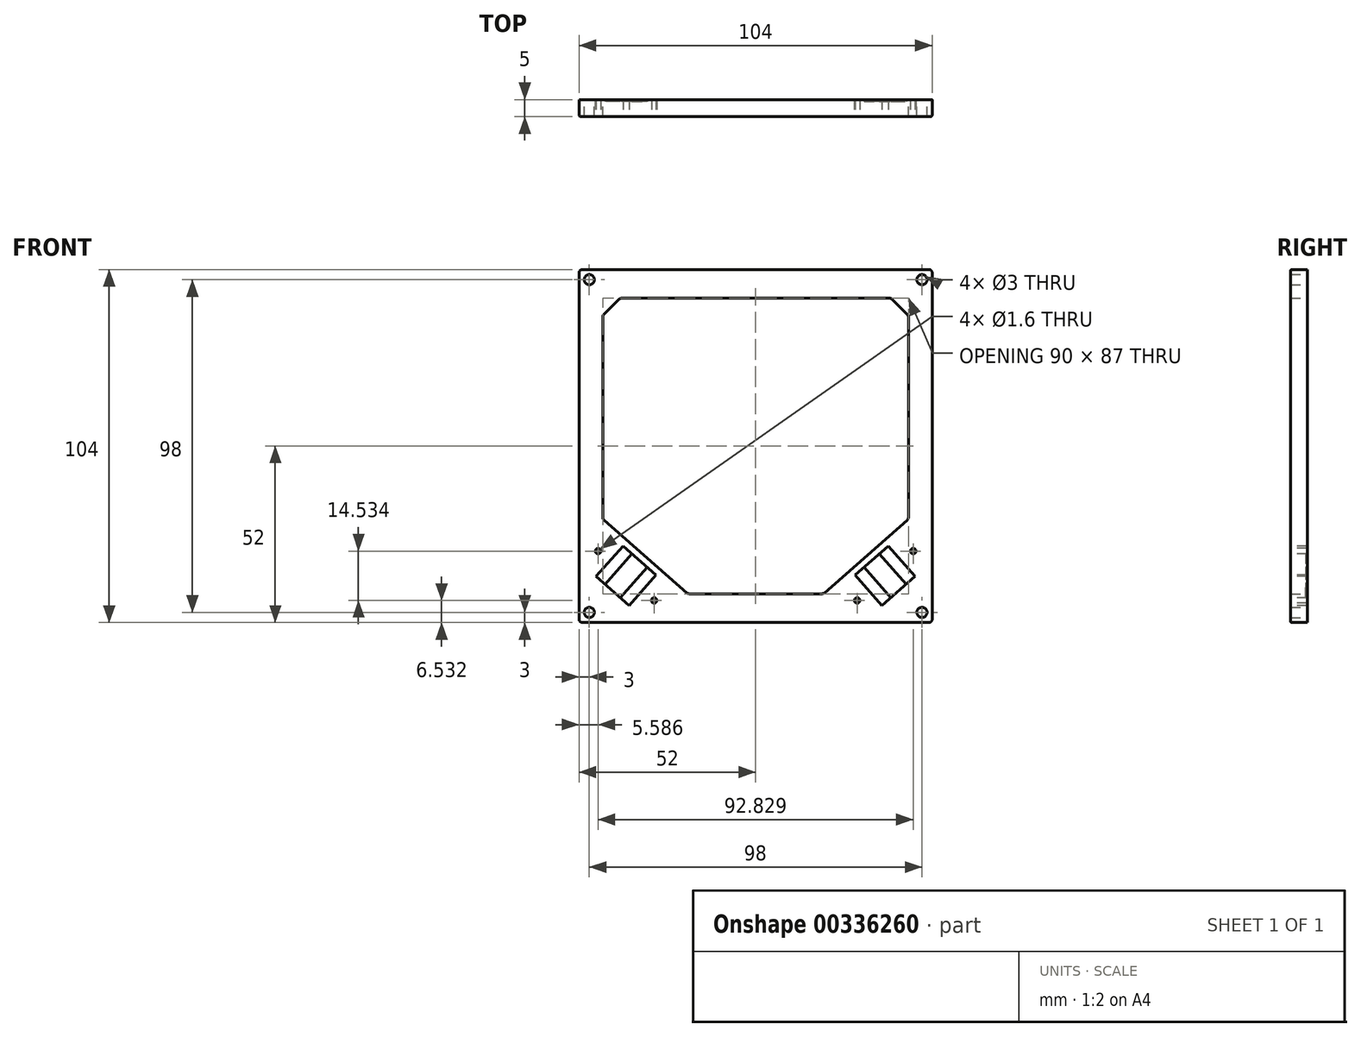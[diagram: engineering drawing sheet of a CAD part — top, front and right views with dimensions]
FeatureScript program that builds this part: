
annotation { "Feature Type Name" : "Feature", "Feature Type Description" : "" }
export const myFeature = defineFeature(function(context is Context, id is Id, definition is map)
    precondition{}
    {
        {
            var Q0;
            Q0=qCreatedBy(makeId("Front.planeOp"),FACE);
            var sketch = newSketch(context, id + "F0", { "sketchPlane" : qUnion([Q0])});
            skLineSegment(sketch, "E0.bottom", {"start": v(-52, 52) * mm, "end": v(52, 52) * mm});
            skLineSegment(sketch, "E0.top", {"start": v(-52, -52) * mm, "end": v(52, -52) * mm});
            skLineSegment(sketch, "E0.left", {"start": v(-52, 52) * mm, "end": v(-52, -52) * mm});
            skLineSegment(sketch, "E0.right", {"start": v(52, 52) * mm, "end": v(52, -52) * mm});
            skCircle(sketch, "E1", {"center": v(-49, 49) * mm, "radius": 1.5 * mm});
            skCircle(sketch, "E2", {"center": v(49, 49) * mm, "radius": 1.5 * mm});
            skCircle(sketch, "E3", {"center": v(-49, -49) * mm, "radius": 1.5 * mm});
            skCircle(sketch, "E4", {"center": v(49, -49) * mm, "radius": 1.5 * mm});
            skCircle(sketch, "E5", {"center": v(-41, -41) * mm, "radius": 2.5 * mm, "construction": true});
            skCircle(sketch, "E6", {"center": v(41, -41) * mm, "radius": 2.5 * mm, "construction": true});
            skSolve(sketch);
        }
        {
            var Q0;
            Q0=makeQuery(id+"F0.imprint","IMPRINT",FACE,{"disambiguationData":[TD([[makeQuery(id+"F0.imprint","IMPRINT",EDGE,{"derivedFrom":sQuery(id+"F0.wireOp",EDGE,"E0.bottom")}),-1.0]])]});
            extrude(context, id + "F1", {"entities" : qUnion([Q0]), "depth" : 5 * mm});
        }
        {
            var Q0;
            Q0=qCreatedBy(makeId("Front.planeOp"),FACE);
            var sketch = newSketch(context, id + "F2", { "sketchPlane" : qUnion([Q0])});
            skLineSegment(sketch, "E7", {"start": v(-40, 43.5) * mm, "end": v(40, 43.5) * mm});
            skLineSegment(sketch, "E8", {"start": v(40, 43.5) * mm, "end": v(45, 38.5) * mm});
            skLineSegment(sketch, "E9", {"start": v(45, 38.5) * mm, "end": v(45, -21.5) * mm});
            skLineSegment(sketch, "E10", {"start": v(45, -21.5) * mm, "end": v(20, -43.5) * mm});
            skLineSegment(sketch, "E11", {"start": v(20, -43.5) * mm, "end": v(-20, -43.5) * mm});
            skLineSegment(sketch, "E12", {"start": v(-20, -43.5) * mm, "end": v(-45, -21.5) * mm});
            skLineSegment(sketch, "E13", {"start": v(-45, -21.5) * mm, "end": v(-45, 38.5) * mm});
            skLineSegment(sketch, "E14", {"start": v(-45, 38.5) * mm, "end": v(-40, 43.5) * mm});
            skSolve(sketch);
        }
        {
            var Q0;
            Q0=qSketchRegion(id+"F2",true);
            var Q1;
            Q1=makeQuery(id+"F1.opExtrude","CAP_FACE",FACE,{"disambiguationData":[OSD([sQuery(id+"F0.wireOp",EDGE,"E0.bottom"),sQuery(id+"F0.wireOp",EDGE,"E0.top"),sQuery(id+"F0.wireOp",EDGE,"E0.left"),sQuery(id+"F0.wireOp",EDGE,"E0.right"),sQuery(id+"F0.wireOp",EDGE,"E1"),sQuery(id+"F0.wireOp",EDGE,"E2"),sQuery(id+"F0.wireOp",EDGE,"E3"),sQuery(id+"F0.wireOp",EDGE,"E4")])],"isStart":false});
            extrude(context, id + "F3", {"entities" : qUnion([Q0, Q1]), "operationType" : NewBodyOperationType.REMOVE, "depth" : 25 * mm});
        }
        {
            var Q0;
            Q0=makeQuery(id+"F1.opExtrude","CAP_FACE",FACE,{"disambiguationData":[OSD([sQuery(id+"F0.wireOp",EDGE,"E0.bottom"),sQuery(id+"F0.wireOp",EDGE,"E0.top"),sQuery(id+"F0.wireOp",EDGE,"E0.left"),sQuery(id+"F0.wireOp",EDGE,"E0.right"),sQuery(id+"F0.wireOp",EDGE,"E1"),sQuery(id+"F0.wireOp",EDGE,"E2"),sQuery(id+"F0.wireOp",EDGE,"E3"),sQuery(id+"F0.wireOp",EDGE,"E4")])],"isStart":false});
            var sketch = newSketch(context, id + "F4", { "sketchPlane" : qUnion([Q0])});
            skLineSegment(sketch, "E15", {"start": v(-39.07, -29.4) * mm, "end": v(-29.31, -38) * mm});
            skLineSegment(sketch, "E16", {"start": v(-29.31, -38) * mm, "end": v(-37.24, -47) * mm});
            skLineSegment(sketch, "E17", {"start": v(-37.24, -47) * mm, "end": v(-47, -38.41) * mm});
            skLineSegment(sketch, "E18", {"start": v(-47, -38.41) * mm, "end": v(-39.07, -29.4) * mm});
            skCircle(sketch, "E19", {"center": v(-46.41, -30.93) * mm, "radius": 1 * mm, "construction": true});
            skCircle(sketch, "E20", {"center": v(-29.9, -45.47) * mm, "radius": 1 * mm, "construction": true});
            skLineSegment(sketch, "E21", {"start": v(-41.1, -24.93) * mm, "end": v(-15.3, -47.64) * mm, "construction": true});
            skLineSegment(sketch, "E22", {"start": v(0, -14.2) * mm, "end": v(0, -66.24) * mm, "construction": true});
            skCircle(sketch, "E23.MirrorC", {"center": v(29.9, -45.47) * mm, "radius": 1 * mm, "construction": true});
            skCircle(sketch, "E24.MirrorC", {"center": v(46.41, -30.93) * mm, "radius": 1 * mm, "construction": true});
            skLineSegment(sketch, "E25.MirrorCS", {"start": v(39.07, -29.4) * mm, "end": v(29.31, -38) * mm});
            skLineSegment(sketch, "E26.MirrorCS", {"start": v(47, -38.41) * mm, "end": v(39.07, -29.4) * mm});
            skLineSegment(sketch, "E27.MirrorCS", {"start": v(37.24, -47) * mm, "end": v(47, -38.41) * mm});
            skLineSegment(sketch, "E28.MirrorCS", {"start": v(29.31, -38) * mm, "end": v(37.24, -47) * mm});
            skSolve(sketch);
        }
        {
            var Q0;
            Q0 = qSketchRegion(id + "F4", true);
            extrude(context, id + "F5", {"entities" : qUnion([Q0]), "operationType" : NewBodyOperationType.REMOVE, "oppositeDirection" : true, "depth" : 4.5 * mm});
        }
        {
            var Q0;
            Q0=makeQuery(id+"F5.boolean.opBoolean","COPY",FACE,{"derivedFrom":makeQuery(id+"F5.opExtrude","CAP_FACE",FACE,{"disambiguationData":[OSD([sQuery(id+"F4.wireOp",EDGE,"E15"),sQuery(id+"F4.wireOp",EDGE,"E16"),sQuery(id+"F4.wireOp",EDGE,"E17"),sQuery(id+"F4.wireOp",EDGE,"E18")])],"isStart":false})});
            var sketch = newSketch(context, id + "F6", { "sketchPlane" : qUnion([Q0])});
            skLineSegment(sketch, "E29", {"start": v(-47, -38.41) * mm, "end": v(-39.07, -29.4) * mm});
            skLineSegment(sketch, "E30", {"start": v(-39.07, -29.4) * mm, "end": v(-36.44, -31.72) * mm});
            skLineSegment(sketch, "E31", {"start": v(-36.44, -31.72) * mm, "end": v(-44.37, -40.72) * mm});
            skLineSegment(sketch, "E32", {"start": v(-44.37, -40.72) * mm, "end": v(-47, -38.41) * mm});
            skLineSegment(sketch, "E33", {"start": v(-31.94, -35.68) * mm, "end": v(-39.87, -44.69) * mm});
            skLineSegment(sketch, "E34", {"start": v(-39.87, -44.69) * mm, "end": v(-37.24, -47) * mm});
            skLineSegment(sketch, "E35", {"start": v(-37.24, -47) * mm, "end": v(-29.31, -38) * mm});
            skLineSegment(sketch, "E36", {"start": v(-29.31, -38) * mm, "end": v(-31.94, -35.68) * mm});
            skLineSegment(sketch, "E37", {"start": v(0, -27.95) * mm, "end": v(0, -63.87) * mm, "construction": true});
            skLineSegment(sketch, "E38.MirrorCS", {"start": v(29.31, -38) * mm, "end": v(31.94, -35.68) * mm});
            skLineSegment(sketch, "E39.MirrorCS", {"start": v(44.37, -40.72) * mm, "end": v(47, -38.41) * mm});
            skLineSegment(sketch, "E40.MirrorCS", {"start": v(39.07, -29.4) * mm, "end": v(36.44, -31.72) * mm});
            skLineSegment(sketch, "E41.MirrorCS", {"start": v(39.87, -44.69) * mm, "end": v(37.24, -47) * mm});
            skLineSegment(sketch, "E42.MirrorCS", {"start": v(47, -38.41) * mm, "end": v(39.07, -29.4) * mm});
            skLineSegment(sketch, "E43.MirrorCS", {"start": v(37.24, -47) * mm, "end": v(29.31, -38) * mm});
            skLineSegment(sketch, "E44.MirrorCS", {"start": v(31.94, -35.68) * mm, "end": v(39.87, -44.69) * mm});
            skLineSegment(sketch, "E45.MirrorCS", {"start": v(36.44, -31.72) * mm, "end": v(44.37, -40.72) * mm});
            skSolve(sketch);
        }
        {
            var Q0;
            Q0 = qSketchRegion(id + "F6", true);
            extrude(context, id + "F7", {"entities" : qUnion([Q0]), "operationType" : NewBodyOperationType.REMOVE, "oppositeDirection" : true, "depth" : 2 * mm});
        }
        {
            var Q0;
            Q0=sQuery(id+"F4.wireOp",VERTEX,"E19.center");
            var Q1;
            Q1=sQuery(id+"F4.wireOp",VERTEX,"E20.center");
            var Q2;
            Q2=sQuery(id+"F4.wireOp",VERTEX,"E23.MirrorC.center");
            var Q3;
            Q3=sQuery(id+"F4.wireOp",VERTEX,"E24.MirrorC.center");
            var Q4;
            Q4=makeQuery(id+"F1.opExtrude","SWEPT_BODY",BODY,{"disambiguationData":[OSD([sQuery(id+"F0.wireOp",EDGE,"E0.bottom"),sQuery(id+"F0.wireOp",EDGE,"E0.top"),sQuery(id+"F0.wireOp",EDGE,"E0.left"),sQuery(id+"F0.wireOp",EDGE,"E0.right"),sQuery(id+"F0.wireOp",EDGE,"E1"),sQuery(id+"F0.wireOp",EDGE,"E2"),sQuery(id+"F0.wireOp",EDGE,"E3"),sQuery(id+"F0.wireOp",EDGE,"E4")])]});
            hole(context, id + "F8", {"style" : HoleStyle.SIMPLE, "endStyle" : HoleEndStyle.BLIND, "holeDiameter" : 1.6 * mm, "holeDepth" : 15 * mm, "tappedDepth" : 12 * mm, "tapClearance" : 3, "locations" : qUnion([Q0, Q1, Q2, Q3]), "scope" : qUnion([Q4])});
        }
        {
            var Q0;
            Q0=makeQuery(id+"F1.opExtrude","SWEPT_EDGE",EDGE,{"disambiguationData":[OSD([sQuery(id+"F0.wireOp",EDGE,"E0.bottom"),sQuery(id+"F0.wireOp",EDGE,"E0.left")])]});
            var Q1;
            Q1=makeQuery(id+"F1.opExtrude","SWEPT_EDGE",EDGE,{"disambiguationData":[OSD([sQuery(id+"F0.wireOp",EDGE,"E0.bottom"),sQuery(id+"F0.wireOp",EDGE,"E0.right")])]});
            var Q2;
            Q2=makeQuery(id+"F1.opExtrude","SWEPT_EDGE",EDGE,{"disambiguationData":[OSD([sQuery(id+"F0.wireOp",EDGE,"E0.top"),sQuery(id+"F0.wireOp",EDGE,"E0.right")])]});
            var Q3;
            Q3=makeQuery(id+"F1.opExtrude","SWEPT_EDGE",EDGE,{"disambiguationData":[OSD([sQuery(id+"F0.wireOp",EDGE,"E0.top"),sQuery(id+"F0.wireOp",EDGE,"E0.left")])]});
            var Q4;
            Q4=makeQuery(id+"F3.boolean.opBoolean","COPY",EDGE,{"derivedFrom":makeQuery(id+"F3.opExtrude","SWEPT_EDGE",EDGE,{"disambiguationData":[OSD([sQuery(id+"F2.wireOp",EDGE,"E12"),sQuery(id+"F2.wireOp",EDGE,"E13")])]})});
            var Q5;
            Q5=makeQuery(id+"F3.boolean.opBoolean","COPY",EDGE,{"derivedFrom":makeQuery(id+"F3.opExtrude","SWEPT_EDGE",EDGE,{"disambiguationData":[OSD([sQuery(id+"F2.wireOp",EDGE,"E11"),sQuery(id+"F2.wireOp",EDGE,"E12")])]})});
            var Q6;
            Q6=makeQuery(id+"F3.boolean.opBoolean","COPY",EDGE,{"derivedFrom":makeQuery(id+"F3.opExtrude","SWEPT_EDGE",EDGE,{"disambiguationData":[OSD([sQuery(id+"F2.wireOp",EDGE,"E10"),sQuery(id+"F2.wireOp",EDGE,"E11")])]})});
            var Q7;
            Q7=makeQuery(id+"F3.boolean.opBoolean","COPY",EDGE,{"derivedFrom":makeQuery(id+"F3.opExtrude","SWEPT_EDGE",EDGE,{"disambiguationData":[OSD([sQuery(id+"F2.wireOp",EDGE,"E9"),sQuery(id+"F2.wireOp",EDGE,"E10")])]})});
            var Q8;
            Q8=makeQuery(id+"F3.boolean.opBoolean","COPY",EDGE,{"derivedFrom":makeQuery(id+"F3.opExtrude","SWEPT_EDGE",EDGE,{"disambiguationData":[OSD([sQuery(id+"F2.wireOp",EDGE,"E13"),sQuery(id+"F2.wireOp",EDGE,"E14")])]})});
            var Q9;
            Q9=makeQuery(id+"F3.boolean.opBoolean","COPY",EDGE,{"derivedFrom":makeQuery(id+"F3.opExtrude","SWEPT_EDGE",EDGE,{"disambiguationData":[OSD([sQuery(id+"F2.wireOp",EDGE,"E7"),sQuery(id+"F2.wireOp",EDGE,"E14")])]})});
            var Q10;
            Q10=makeQuery(id+"F3.boolean.opBoolean","COPY",EDGE,{"derivedFrom":makeQuery(id+"F3.opExtrude","SWEPT_EDGE",EDGE,{"disambiguationData":[OSD([sQuery(id+"F2.wireOp",EDGE,"E7"),sQuery(id+"F2.wireOp",EDGE,"E8")])]})});
            var Q11;
            Q11=makeQuery(id+"F3.boolean.opBoolean","COPY",EDGE,{"derivedFrom":makeQuery(id+"F3.opExtrude","SWEPT_EDGE",EDGE,{"disambiguationData":[OSD([sQuery(id+"F2.wireOp",EDGE,"E8"),sQuery(id+"F2.wireOp",EDGE,"E9")])]})});
            fillet(context, id + "F9", {"entities" : qUnion([Q0, Q1, Q2, Q3, Q4, Q5, Q6, Q7, Q8, Q9, Q10, Q11]), "radius" : 1 * mm, "tangentPropagation" : true, "allowEdgeOverflow" : false});
        }
        {
            var Q0;
            Q0=makeQuery(id+"F1.opExtrude","CAP_EDGE",EDGE,{"disambiguationData":[OSD([sQuery(id+"F0.wireOp",EDGE,"E0.top")])],"isStart":false});
            fillet(context, id + "F10", {"entities" : qUnion([Q0]), "radius" : 0.5 * mm, "tangentPropagation" : true, "allowEdgeOverflow" : false});
        }
    });
